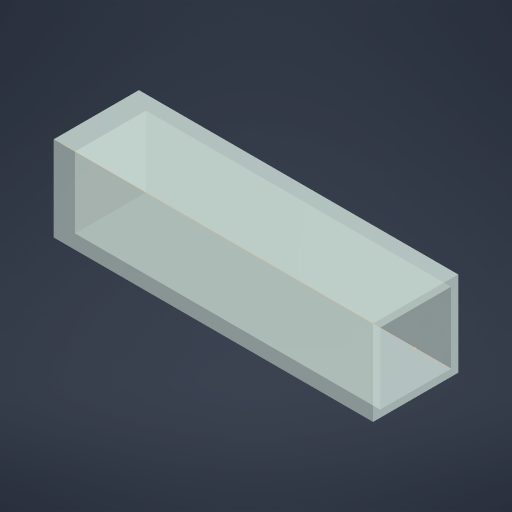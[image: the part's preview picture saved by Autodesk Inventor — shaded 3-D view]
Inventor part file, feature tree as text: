
AUTODESK INVENTOR PART (.ipt)
format: ipt  version: 2024.1 (Build 281209000, 209)  size: 171,520 bytes
history: native  units: mm
features: extrude x2, other x2, sketch x2
ambient origin geometry x8: Origin, YZ Plane, XZ Plane, XY Plane, X Axis, Y Axis, Z Axis, Center Point
bodies: Solid1 (feature_tree)
feature tree (6):
  extrude  "Extrusion1"  Depth=12.0mm
  extrude  "Extrusion2"  Depth=10.0mm
  other  "Work Axis1"
  sketch  "Sketch1"  dims[d0=12.0mm d1=12.0mm]
  sketch  "Sketch2"  dims[d2=45.0mm d3=0.0mm d4=10.0mm d5=10.0mm d6=43.0mm d7=0.0mm]
  other  "Work Point2"
